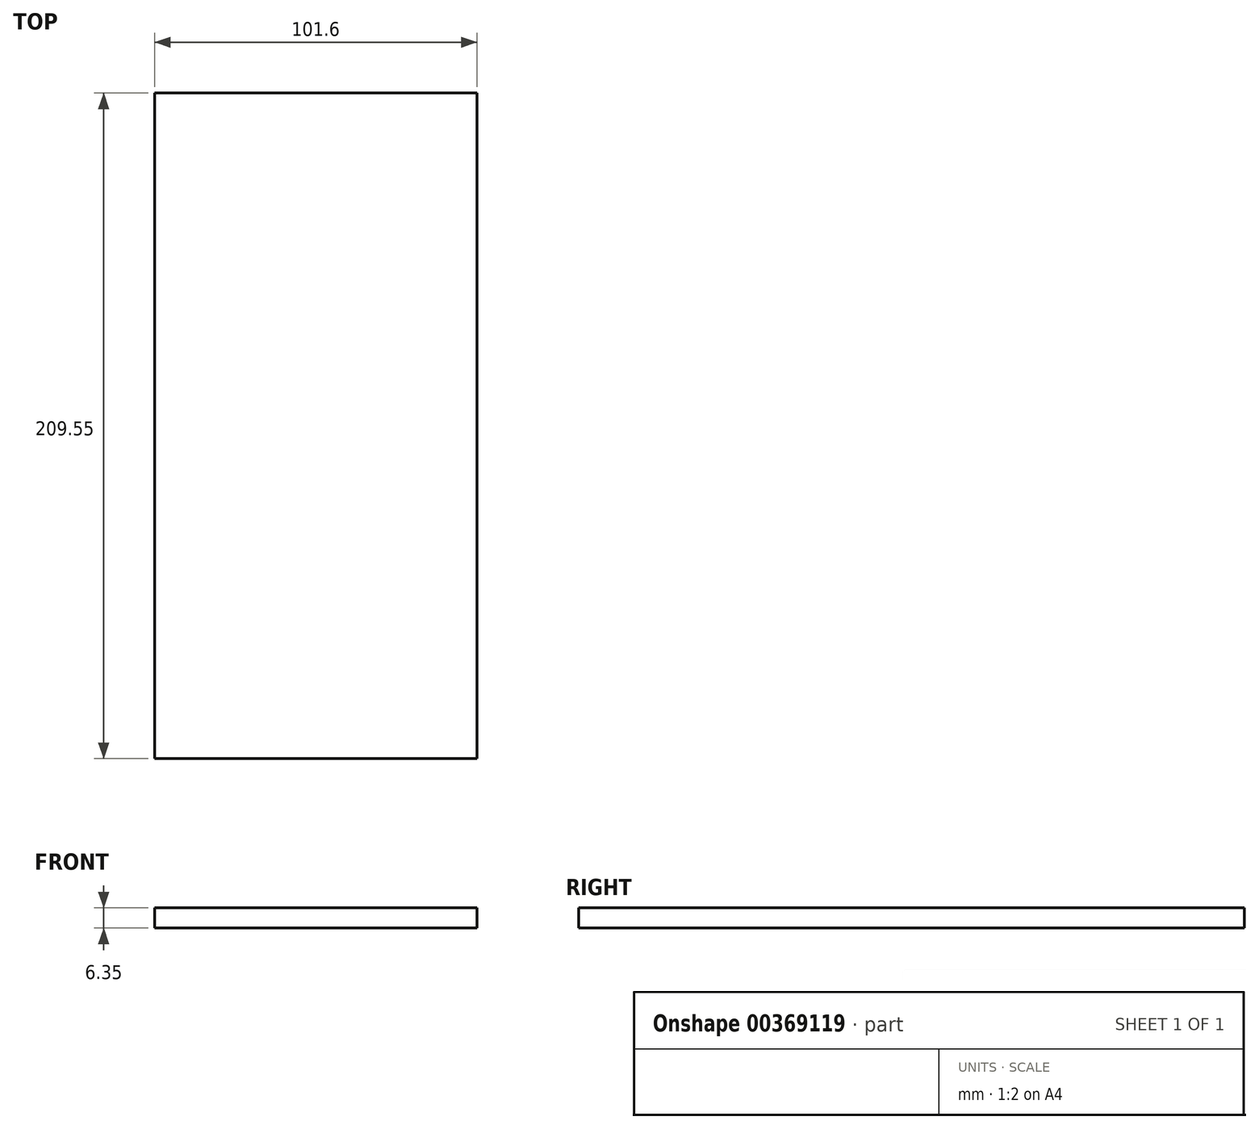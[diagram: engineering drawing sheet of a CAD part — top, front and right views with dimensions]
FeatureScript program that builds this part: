
annotation { "Feature Type Name" : "Feature", "Feature Type Description" : "" }
export const myFeature = defineFeature(function(context is Context, id is Id, definition is map)
    precondition{}
    {
        {
            var Q0;
            Q0=qCreatedBy(makeId("Top.planeOp"),FACE);
            var sketch = newSketch(context, id + "F0", { "sketchPlane" : qUnion([Q0])});
            skLineSegment(sketch, "E0.bottom", {"start": v(0, 0) * mm, "end": v(101.6, 0) * mm});
            skLineSegment(sketch, "E0.top", {"start": v(0, -209.55) * mm, "end": v(101.6, -209.55) * mm});
            skLineSegment(sketch, "E0.left", {"start": v(0, 0) * mm, "end": v(0, -209.55) * mm});
            skLineSegment(sketch, "E0.right", {"start": v(101.6, 0) * mm, "end": v(101.6, -209.55) * mm});
            skSolve(sketch);
        }
        {
            var Q0;
            Q0=makeQuery(id+"F0.imprint","IMPRINT",FACE,{"disambiguationData":[TD([[makeQuery(id+"F0.imprint","IMPRINT",EDGE,{"derivedFrom":sQuery(id+"F0.wireOp",EDGE,"E0.bottom")}),-1.0]])]});
            extrude(context, id + "F1", {"entities" : qUnion([Q0]), "depth" : 6.35 * mm});
        }
    });
